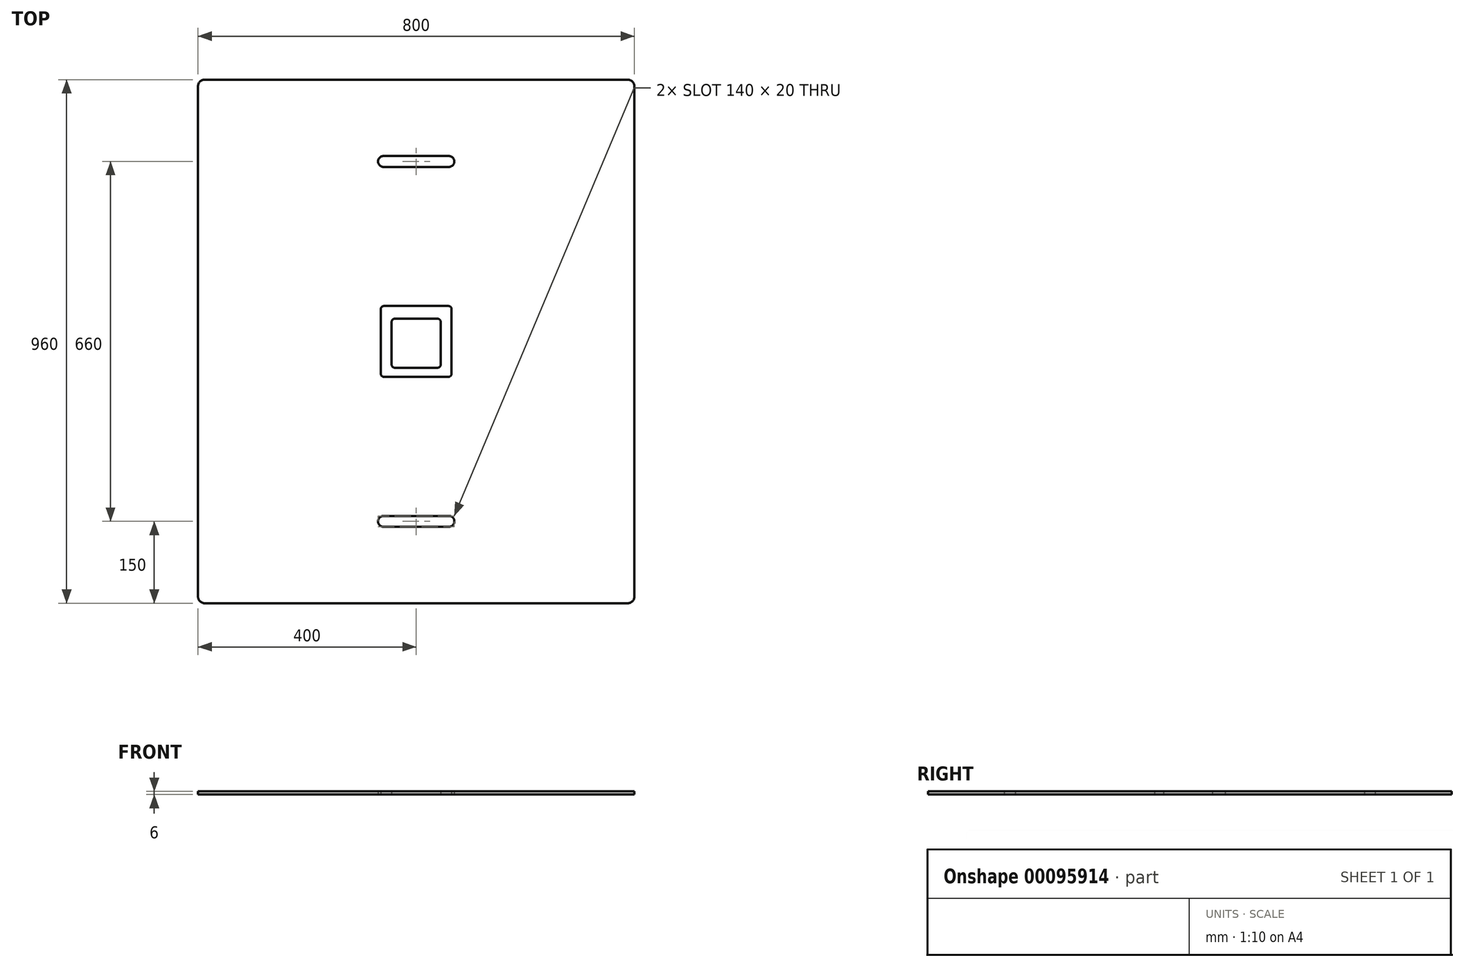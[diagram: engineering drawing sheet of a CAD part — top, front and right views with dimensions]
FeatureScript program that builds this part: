
annotation { "Feature Type Name" : "Feature", "Feature Type Description" : "" }
export const myFeature = defineFeature(function(context is Context, id is Id, definition is map)
    precondition{}
    {
        {
            var Q0;
            Q0=qCreatedBy(makeId("Top.planeOp"),FACE);
            var sketch = newSketch(context, id + "F0", { "sketchPlane" : qUnion([Q0])});
            skLineSegment(sketch, "E0.bottom", {"start": v(-39, 41.66) * mm, "end": v(39, 41.66) * mm});
            skLineSegment(sketch, "E0.top", {"start": v(-39, -48.34) * mm, "end": v(39, -48.34) * mm});
            skLineSegment(sketch, "E0.left", {"start": v(-45, 35.66) * mm, "end": v(-45, -42.34) * mm});
            skLineSegment(sketch, "E0.right", {"start": v(45, 35.66) * mm, "end": v(45, -42.34) * mm});
            skPoint(sketch, "E0.middle", {"position": v(0, -3.34) * mm});
            skPoint(sketch, "E1.visualSharp", {"position": v(-45, 41.66) * mm});
            skArc(sketch, "E1.filletArc", {"start": v(-39, 41.66) * mm, "mid": v(-43.24, 39.9) * mm, "end": v(-45, 35.66) * mm});
            skPoint(sketch, "E2.visualSharp", {"position": v(45, 41.66) * mm});
            skArc(sketch, "E2.filletArc", {"start": v(45, 35.66) * mm, "mid": v(43.24, 39.9) * mm, "end": v(39, 41.66) * mm});
            skPoint(sketch, "E3.visualSharp", {"position": v(45, -48.34) * mm});
            skArc(sketch, "E3.filletArc", {"start": v(39, -48.34) * mm, "mid": v(43.24, -46.58) * mm, "end": v(45, -42.34) * mm});
            skPoint(sketch, "E4.visualSharp", {"position": v(-45, -48.34) * mm});
            skArc(sketch, "E4.filletArc", {"start": v(-45, -42.34) * mm, "mid": v(-43.24, -46.58) * mm, "end": v(-39, -48.34) * mm});
            skSolve(sketch);
        }
        {
            var Q0;
            Q0=makeQuery(id+"F0.imprint","IMPRINT",FACE,{"disambiguationData":[TD([[makeQuery(id+"F0.imprint","IMPRINT",EDGE,{"derivedFrom":sQuery(id+"F0.wireOp",EDGE,"E0.bottom")}),-1.0]])]});
            extrude(context, id + "F1", {"entities" : qUnion([Q0]), "flatOperationType" : FlatOperationType.REMOVE, "offsetDistance" : 25 * mm, "depth" : 6 * mm, "domain" : OperationDomain.MODEL});
        }
        {
            var Q0;
            Q0=qCreatedBy(makeId("Top.planeOp"),FACE);
            var sketch = newSketch(context, id + "F2", { "sketchPlane" : qUnion([Q0])});
            skLineSegment(sketch, "E5.bottom", {"start": v(59, 65) * mm, "end": v(-59, 65) * mm});
            skLineSegment(sketch, "E5.top", {"start": v(59, -65) * mm, "end": v(-59, -65) * mm});
            skLineSegment(sketch, "E5.left", {"start": v(65, 59) * mm, "end": v(65, -59) * mm});
            skLineSegment(sketch, "E5.right", {"start": v(-65, 59) * mm, "end": v(-65, -59) * mm});
            skPoint(sketch, "E5.middle", {"position": v(0, 0) * mm});
            skPoint(sketch, "E6.visualSharp", {"position": v(65, 65) * mm});
            skArc(sketch, "E6.filletArc", {"start": v(65, 59) * mm, "mid": v(63.24, 63.24) * mm, "end": v(59, 65) * mm});
            skPoint(sketch, "E7.visualSharp", {"position": v(65, -65) * mm});
            skArc(sketch, "E7.filletArc", {"start": v(59, -65) * mm, "mid": v(63.24, -63.24) * mm, "end": v(65, -59) * mm});
            skPoint(sketch, "E8.visualSharp", {"position": v(-65, -65) * mm});
            skArc(sketch, "E8.filletArc", {"start": v(-65, -59) * mm, "mid": v(-63.24, -63.24) * mm, "end": v(-59, -65) * mm});
            skPoint(sketch, "E9.visualSharp", {"position": v(-65, 65) * mm});
            skArc(sketch, "E9.filletArc", {"start": v(-59, 65) * mm, "mid": v(-63.24, 63.24) * mm, "end": v(-65, 59) * mm});
            skSolve(sketch);
        }
        {
            var Q0;
            Q0 = qSketchRegion(id + "F2", true);
            extrude(context, id + "F3", {"entities" : qUnion([Q0]), "depth" : 6 * mm});
        }
        {
            var Q0;
            Q0=qCreatedBy(makeId("Top.planeOp"),FACE);
            var sketch = newSketch(context, id + "F4", { "sketchPlane" : qUnion([Q0])});
            skLineSegment(sketch, "E10.bottom", {"start": v(-388, 480) * mm, "end": v(388, 480) * mm});
            skLineSegment(sketch, "E10.top", {"start": v(-388, -480) * mm, "end": v(388, -480) * mm});
            skLineSegment(sketch, "E10.left", {"start": v(-400, 468) * mm, "end": v(-400, -468) * mm});
            skLineSegment(sketch, "E10.right", {"start": v(400, 468) * mm, "end": v(400, -468) * mm});
            skPoint(sketch, "E10.middle", {"position": v(0, 0) * mm});
            skLineSegment(sketch, "E11", {"start": v(0, 320) * mm, "end": v(0, 340) * mm, "construction": true});
            skArc(sketch, "E12", {"start": v(-60, 340) * mm, "mid": v(-70, 330) * mm, "end": v(-60, 320) * mm});
            skPoint(sketch, "E13.visualSharp", {"position": v(-400, 480) * mm});
            skArc(sketch, "E13.filletArc", {"start": v(-388, 480) * mm, "mid": v(-396.49, 476.49) * mm, "end": v(-400, 468) * mm});
            skPoint(sketch, "E14.visualSharp", {"position": v(400, 480) * mm});
            skArc(sketch, "E14.filletArc", {"start": v(400, 468) * mm, "mid": v(396.49, 476.49) * mm, "end": v(388, 480) * mm});
            skPoint(sketch, "E15.visualSharp", {"position": v(400, -480) * mm});
            skArc(sketch, "E15.filletArc", {"start": v(388, -480) * mm, "mid": v(396.49, -476.49) * mm, "end": v(400, -468) * mm});
            skPoint(sketch, "E16.visualSharp", {"position": v(-400, -480) * mm});
            skArc(sketch, "E16.filletArc", {"start": v(-400, -468) * mm, "mid": v(-396.49, -476.49) * mm, "end": v(-388, -480) * mm});
            skArc(sketch, "E17.MirrorC", {"start": v(60, 340) * mm, "mid": v(70, 330) * mm, "end": v(60, 320) * mm});
            skLineSegment(sketch, "E18", {"start": v(60, 340) * mm, "end": v(-60, 340) * mm});
            skLineSegment(sketch, "E19", {"start": v(60, 320) * mm, "end": v(-60, 320) * mm});
            skArc(sketch, "E20.MirrorCS", {"start": v(-60, -340) * mm, "mid": v(-70, -330) * mm, "end": v(-60, -320) * mm});
            skLineSegment(sketch, "E21.MirrorCS", {"start": v(60, -340) * mm, "end": v(-60, -340) * mm});
            skArc(sketch, "E22.MirrorCS", {"start": v(60, -340) * mm, "mid": v(70, -330) * mm, "end": v(60, -320) * mm});
            skLineSegment(sketch, "E23.MirrorCS", {"start": v(60, -320) * mm, "end": v(-60, -320) * mm});
            skPoint(sketch, "E24.orphan", {"position": v(0, 480) * mm});
            skSolve(sketch);
        }
        {
            var Q0;
            Q0=makeQuery(id+"F4.imprint","IMPRINT",FACE,{"disambiguationData":[TD([[makeQuery(id+"F4.imprint","IMPRINT",EDGE,{"derivedFrom":sQuery(id+"F4.wireOp",EDGE,"E10.bottom")}),-1.0]])]});
            extrude(context, id + "F5", {"entities" : qUnion([Q0]), "depth" : 6 * mm});
        }
    });
